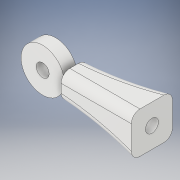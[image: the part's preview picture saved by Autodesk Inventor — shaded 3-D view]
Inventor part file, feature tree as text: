
AUTODESK INVENTOR PART (.ipt)
format: ipt  version: 2017 SP1 (Build 210196100, 196)  size: 208,384 bytes
history: native  units: in
note: dims shown in document units (in); Inventor stores cm internally (conversion verified against a paired STEP export)
features: extrude x7, sketch x7, projected_geometry x2, fillet x1
ambient origin geometry x8: Origin, YZ Plane, XZ Plane, XY Plane, X Axis, Y Axis, Z Axis, Center Point
bodies: Solid1 (feature_tree)
feature tree (17):
  extrude  "Extrusion1"  Depth=0.3937in
  extrude  "Extrusion2"  Depth=0.0394in
  extrude  "Extrusion3"  Depth=0.1181in
  extrude  "Extrusion4"  Depth=0.2362in
  extrude  "Extrusion5"  Depth=0.374in
  extrude  "Extrusion6"  Depth=5.9055in
  fillet  "Fillet1"  Radius=0.2362in
  extrude  "Extrusion7"  Depth=0.3937in
  sketch  "Sketch1"  dims[d0=0.1181in d1=0.3937in]
  sketch  "Sketch2"  dims[d2=0.1181in d3=0.0in d4=0.0394in]
  sketch  "Sketch3"  dims[d6=0.1181in d7=0.0in d8=0.1181in]
  sketch  "Sketch4"  dims[d9=0.2362in d10=0.2362in]
  sketch  "Sketch5"  dims[d11=0.7087in d12=0.0in d13=0.374in]
  sketch  "Sketch6"  dims[d14=5.9055in d15=5.9055in d16=0.2362in d17=0.0in]
  projected_geometry  "Projected Loop1"
  projected_geometry  "Projected Loop2"
  sketch  "Sketch7"  dims[d18=0.374in d19=5.9055in d20=5.9055in d21=0.128in d22=0.2461in d23=0.0in d24=0.0in d25=0.128in d26=0.0in d27=0.0787in d28=0.1181in d29=0.3937in d30=0.0in]
